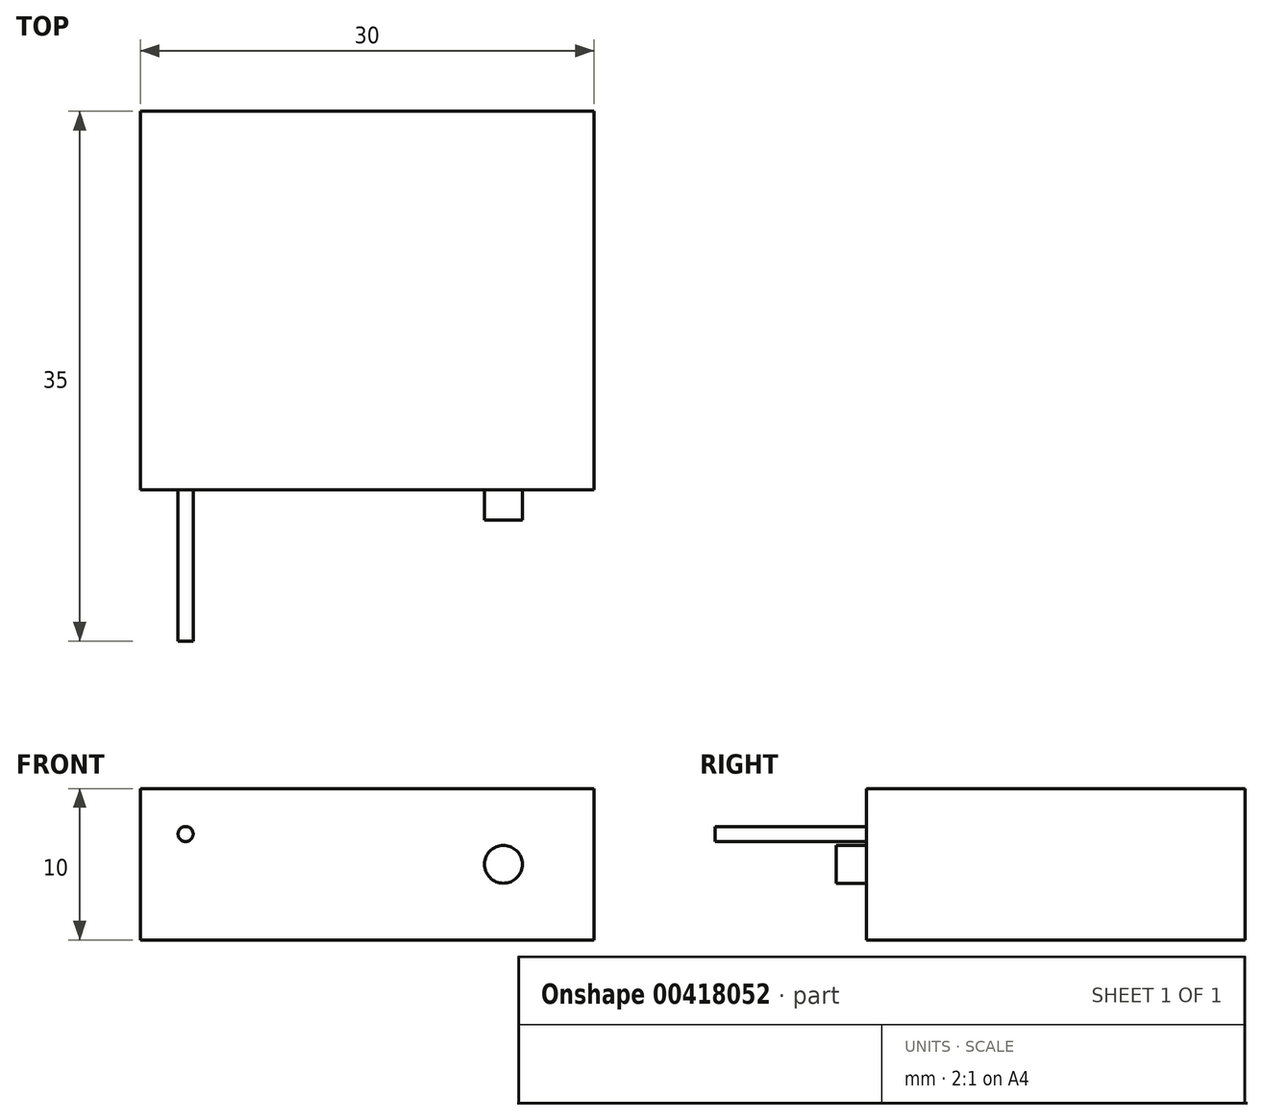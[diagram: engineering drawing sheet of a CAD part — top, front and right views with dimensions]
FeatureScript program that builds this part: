
annotation { "Feature Type Name" : "Feature", "Feature Type Description" : "" }
export const myFeature = defineFeature(function(context is Context, id is Id, definition is map)
    precondition{}
    {
        {
            var Q0;
            Q0=qCreatedBy(makeId("Front.planeOp"),FACE);
            var sketch = newSketch(context, id + "F0", { "sketchPlane" : qUnion([Q0])});
            skLineSegment(sketch, "E0.bottom", {"start": v(-46, 10) * mm, "end": v(-16, 10) * mm});
            skLineSegment(sketch, "E0.top", {"start": v(-46, 0) * mm, "end": v(-16, 0) * mm});
            skLineSegment(sketch, "E0.left", {"start": v(-46, 10) * mm, "end": v(-46, 0) * mm});
            skLineSegment(sketch, "E0.right", {"start": v(-16, 10) * mm, "end": v(-16, 0) * mm});
            skSolve(sketch);
        }
        {
            var Q0;
            Q0 = qSketchRegion(id + "F0", true);
            extrude(context, id + "F1", {"entities" : qUnion([Q0]), "depth" : -25 * mm});
        }
        {
            var Q0;
            Q0=makeQuery(id+"F1.opExtrude","CAP_FACE",FACE,{"disambiguationData":[OSD([sQuery(id+"F0.wireOp",EDGE,"E0.bottom"),sQuery(id+"F0.wireOp",EDGE,"E0.top"),sQuery(id+"F0.wireOp",EDGE,"E0.left"),sQuery(id+"F0.wireOp",EDGE,"E0.right")])],"isStart":true});
            var sketch = newSketch(context, id + "F2", { "sketchPlane" : qUnion([Q0])});
            skCircle(sketch, "E1", {"center": v(-22, 5) * mm, "radius": 1.25 * mm});
            skSolve(sketch);
        }
        {
            var Q0;
            Q0 = qSketchRegion(id + "F2", true);
            extrude(context, id + "F3", {"entities" : qUnion([Q0]), "operationType" : NewBodyOperationType.ADD, "depth" : 2 * mm});
        }
        {
            var Q0;
            Q0=makeQuery(id+"F1.opExtrude","CAP_FACE",FACE,{"disambiguationData":[OSD([sQuery(id+"F0.wireOp",EDGE,"E0.bottom"),sQuery(id+"F0.wireOp",EDGE,"E0.top"),sQuery(id+"F0.wireOp",EDGE,"E0.left"),sQuery(id+"F0.wireOp",EDGE,"E0.right")])],"isStart":true});
            var sketch = newSketch(context, id + "F4", { "sketchPlane" : qUnion([Q0])});
            skCircle(sketch, "E2", {"center": v(-43, 7) * mm, "radius": 0.5 * mm});
            skSolve(sketch);
        }
        {
            var Q0;
            Q0 = qSketchRegion(id + "F4", true);
            extrude(context, id + "F5", {"entities" : qUnion([Q0]), "operationType" : NewBodyOperationType.ADD, "depth" : 10 * mm});
        }
    });
